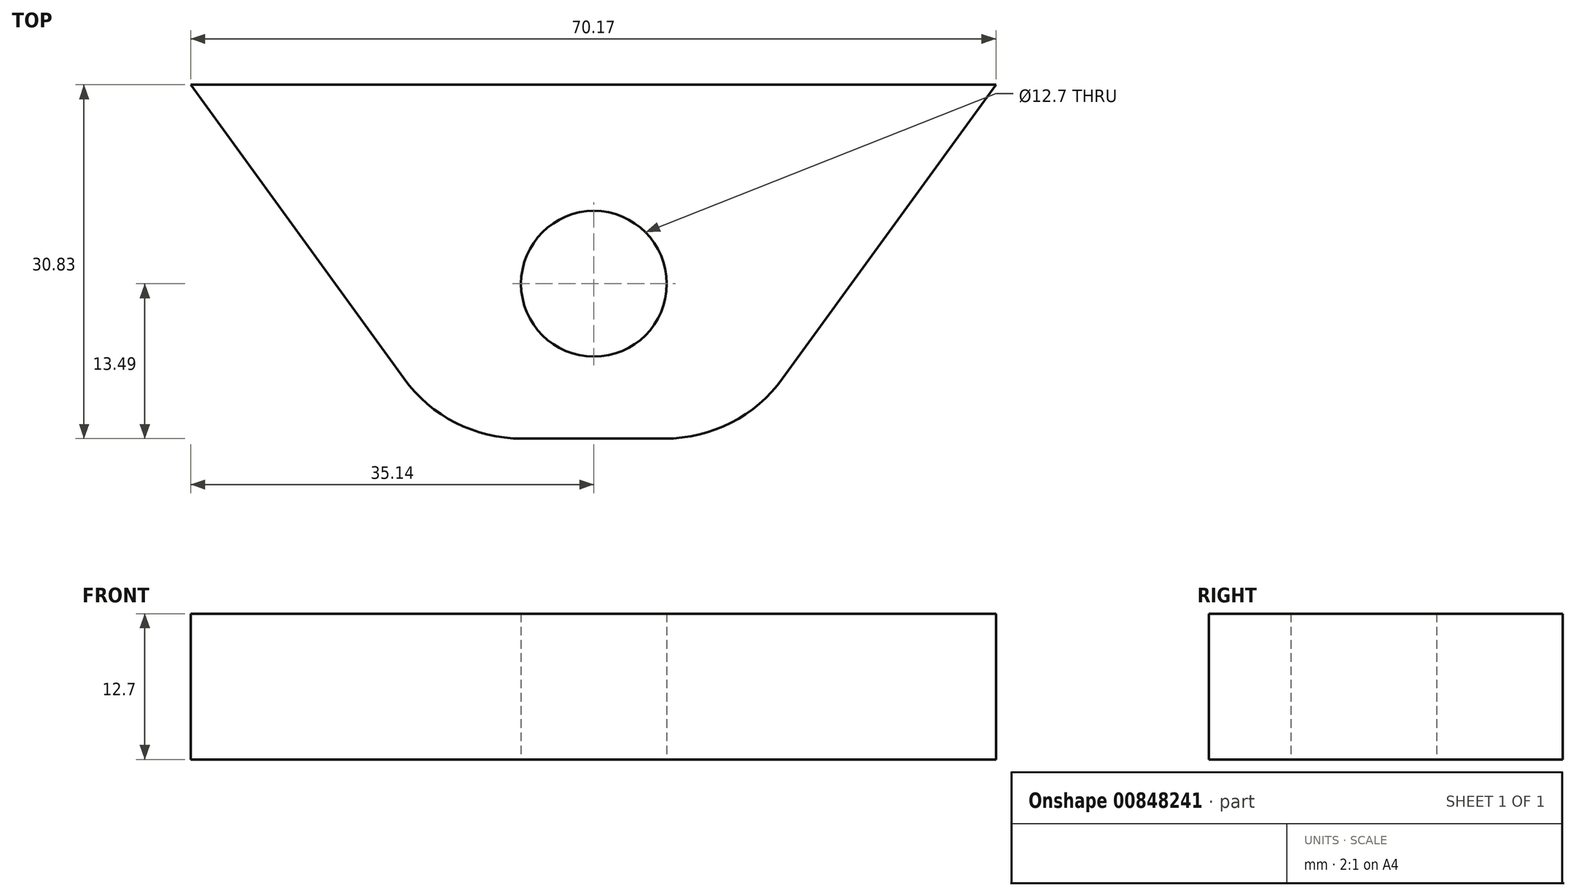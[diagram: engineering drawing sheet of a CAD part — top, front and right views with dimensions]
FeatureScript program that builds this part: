
annotation { "Feature Type Name" : "Feature", "Feature Type Description" : "" }
export const myFeature = defineFeature(function(context is Context, id is Id, definition is map)
    precondition{}
    {
        {
            var Q0;
            Q0=qCreatedBy(makeId("Top.planeOp"),FACE);
            var sketch = newSketch(context, id + "F0", { "sketchPlane" : qUnion([Q0])});
            skLineSegment(sketch, "E0", {"start": v(-35.14, 17.34) * mm, "end": v(35.03, 17.34) * mm});
            skLineSegment(sketch, "E1", {"start": v(-35.14, 17.34) * mm, "end": v(-16.56, -8.25) * mm});
            skLineSegment(sketch, "E2", {"start": v(-6.29, -13.5) * mm, "end": v(6.17, -13.5) * mm});
            skLineSegment(sketch, "E3", {"start": v(16.44, -8.25) * mm, "end": v(35.03, 17.34) * mm});
            skPoint(sketch, "E4.visualSharp", {"position": v(-12.76, -13.5) * mm});
            skArc(sketch, "E4.filletArc", {"start": v(-16.56, -8.25) * mm, "mid": v(-12.05, -12.1) * mm, "end": v(-6.29, -13.5) * mm});
            skPoint(sketch, "E5.visualSharp", {"position": v(12.64, -13.5) * mm});
            skArc(sketch, "E5.filletArc", {"start": v(6.17, -13.5) * mm, "mid": v(11.93, -12.1) * mm, "end": v(16.44, -8.25) * mm});
            skCircle(sketch, "E6", {"center": v(0, 0) * mm, "radius": 6.35 * mm});
            skSolve(sketch);
        }
        {
            var Q0;
            Q0 = qSketchRegion(id + "F0", true);
            extrude(context, id + "F1", {"entities" : qUnion([Q0]), "depth" : 12.7 * mm, "offsetDistance" : 25.4 * mm});
        }
    });
